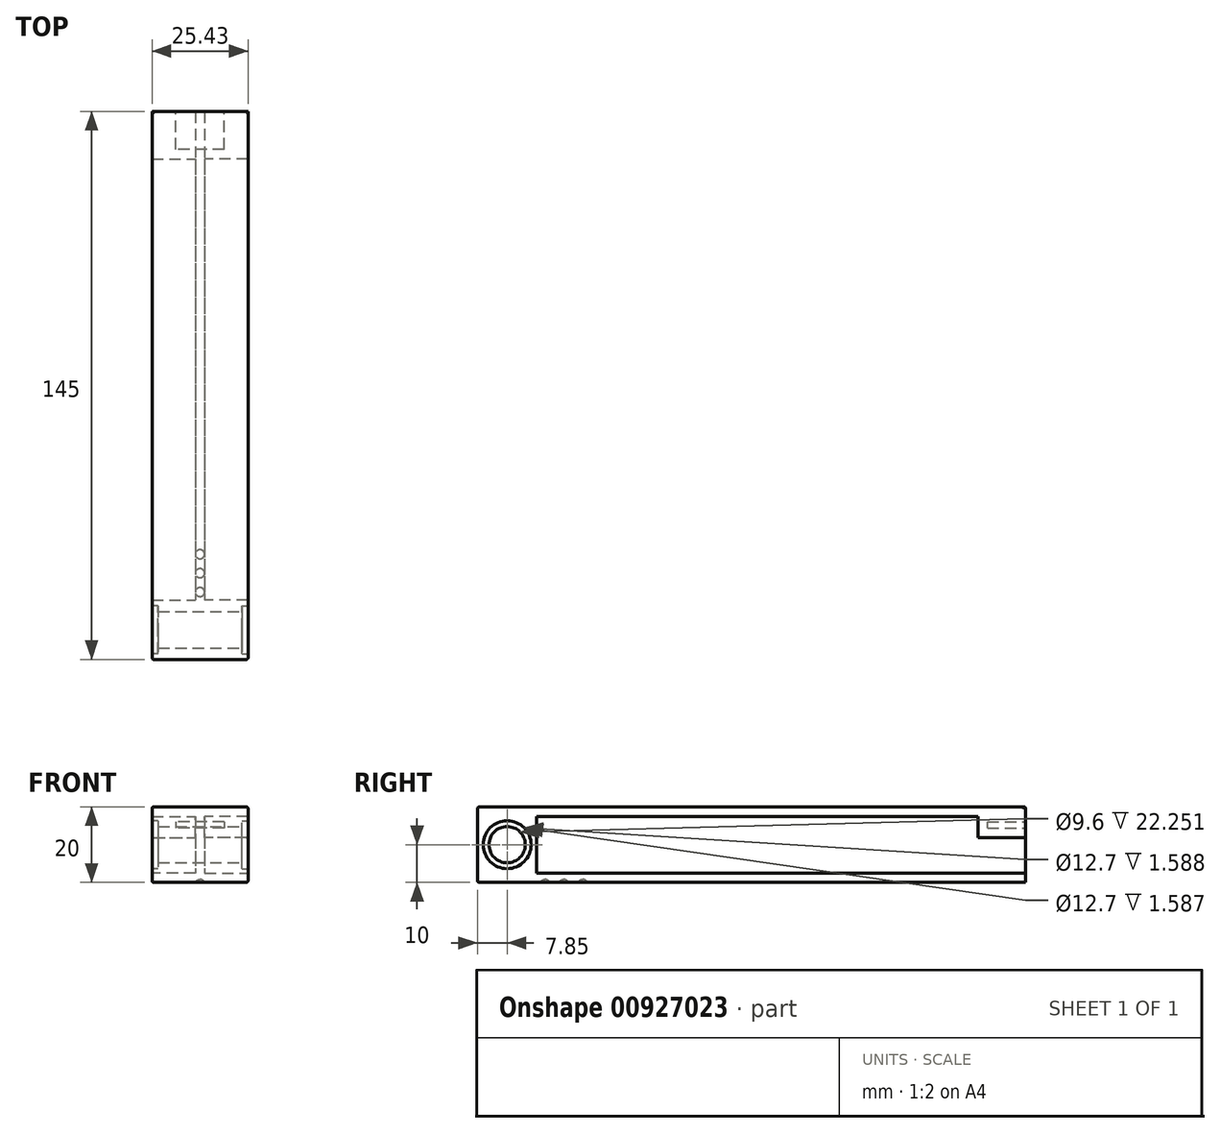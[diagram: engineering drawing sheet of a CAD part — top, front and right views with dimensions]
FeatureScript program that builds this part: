
annotation { "Feature Type Name" : "Feature", "Feature Type Description" : "" }
export const myFeature = defineFeature(function(context is Context, id is Id, definition is map)
    precondition{}
    {
        {
            var Q0;
            Q0=qCreatedBy(makeId("Front.planeOp"),FACE);
            var sketch = newSketch(context, id + "F0", { "sketchPlane" : qUnion([Q0])});
            skLineSegment(sketch, "E0", {"start": v(0, 0) * mm, "end": v(12.71, 0) * mm});
            skLineSegment(sketch, "E1", {"start": v(12.71, 0) * mm, "end": v(12.71, 20) * mm, "construction": true});
            skLineSegment(sketch, "E2", {"start": v(12.71, 20) * mm, "end": v(0, 20) * mm});
            skLineSegment(sketch, "E3", {"start": v(0, 20) * mm, "end": v(0, 17.5) * mm});
            skLineSegment(sketch, "E4", {"start": v(0, 17.5) * mm, "end": v(11.46, 17.5) * mm});
            skLineSegment(sketch, "E5", {"start": v(11.46, 17.5) * mm, "end": v(11.46, 2.5) * mm});
            skLineSegment(sketch, "E6", {"start": v(11.46, 2.5) * mm, "end": v(0, 2.5) * mm});
            skLineSegment(sketch, "E7", {"start": v(0, 2.5) * mm, "end": v(0, 0) * mm});
            skLineSegment(sketch, "E8.MirrorCS", {"start": v(12.71, 20) * mm, "end": v(25.43, 20) * mm});
            skLineSegment(sketch, "E9.MirrorCS", {"start": v(25.43, 20) * mm, "end": v(25.43, 17.5) * mm});
            skLineSegment(sketch, "E10.MirrorCS", {"start": v(25.43, 17.5) * mm, "end": v(13.96, 17.5) * mm});
            skLineSegment(sketch, "E11.MirrorCS", {"start": v(13.96, 17.5) * mm, "end": v(13.96, 2.5) * mm});
            skLineSegment(sketch, "E12.MirrorCS", {"start": v(13.96, 2.5) * mm, "end": v(25.43, 2.5) * mm});
            skLineSegment(sketch, "E13.MirrorCS", {"start": v(25.43, 2.5) * mm, "end": v(25.43, 0) * mm});
            skLineSegment(sketch, "E14.MirrorCS", {"start": v(25.43, 0) * mm, "end": v(12.71, 0) * mm});
            skSolve(sketch);
        }
        {
            var Q0;
            Q0=makeQuery(id+"F0.imprint","IMPRINT",FACE,{"disambiguationData":[TD([[makeQuery(id+"F0.imprint","IMPRINT",EDGE,{"derivedFrom":sQuery(id+"F0.wireOp",EDGE,"E0")}),1.0]])]});
            extrude(context, id + "F1", {"entities" : qUnion([Q0]), "oppositeDirection" : true, "depth" : 145 * mm, "offsetDistance" : 25 * mm});
        }
        {
            var Q0;
            Q0=makeQuery(id+"F1.opExtrude","SWEPT_FACE",FACE,{"disambiguationData":[OSD([sQuery(id+"F0.wireOp",EDGE,"E11.MirrorCS")])]});
            var sketch = newSketch(context, id + "F2", { "sketchPlane" : qUnion([Q0])});
            skLineSegment(sketch, "E15.bottom", {"start": v(0, 17.5) * mm, "end": v(15.7, 17.5) * mm});
            skLineSegment(sketch, "E15.top", {"start": v(0, 2.5) * mm, "end": v(15.7, 2.5) * mm});
            skLineSegment(sketch, "E15.left", {"start": v(0, 17.5) * mm, "end": v(0, 2.5) * mm});
            skLineSegment(sketch, "E15.right", {"start": v(15.7, 17.5) * mm, "end": v(15.7, 2.5) * mm});
            skSolve(sketch);
        }
        {
            var Q0;
            Q0=makeQuery(id+"F2.imprint","IMPRINT",FACE,{"disambiguationData":[TD([[makeQuery(id+"F2.imprint","IMPRINT",EDGE,{"derivedFrom":sQuery(id+"F2.wireOp",EDGE,"E15.bottom")}),1.0]])]});
            var Q1;
            Q1=makeQuery(id+"F1.opExtrude","SWEPT_FACE",FACE,{"disambiguationData":[OSD([sQuery(id+"F0.wireOp",EDGE,"E9.MirrorCS")])]});
            extrude(context, id + "F3", {"entities" : qUnion([Q0]), "operationType" : NewBodyOperationType.ADD, "endBound" : BoundingType.UP_TO_SURFACE, "depth" : 25 * mm, "endBoundEntityFace" : qUnion([Q1]), "offsetDistance" : 25 * mm});
        }
        {
            var Q0;
            Q0=makeQuery(id+"F1.opExtrude","SWEPT_FACE",FACE,{"disambiguationData":[OSD([sQuery(id+"F0.wireOp",EDGE,"E5")])]});
            var sketch = newSketch(context, id + "F4", { "sketchPlane" : qUnion([Q0])});
            skLineSegment(sketch, "E16.0", {"start": v(-15.7, 17.5) * mm, "end": v(-15.7, 2.5) * mm});
            skSolve(sketch);
        }
        {
            var Q0;
            {var subQ0=sQuery(id+"F4.wireOp",EDGE,"E16.0");Q0=makeQuery(id+"F4.imprint","IMPRINT",FACE,{"disambiguationData":[TD([[makeQuery(id+"F4.imprint","IMPRINT",EDGE,{"derivedFrom":subQ0}),1.0]])]});}
            var Q1;
            Q1=makeQuery(id+"F1.opExtrude","SWEPT_FACE",FACE,{"disambiguationData":[OSD([sQuery(id+"F0.wireOp",EDGE,"E3")])]});
            extrude(context, id + "F5", {"entities" : qUnion([Q0]), "operationType" : NewBodyOperationType.ADD, "endBound" : BoundingType.UP_TO_SURFACE, "depth" : 25 * mm, "endBoundEntityFace" : qUnion([Q1]), "offsetDistance" : 25 * mm});
        }
        {
            var Q0;
            Q0=makeQuery(id+"F3.boolean.opBoolean","MERGE",FACE,{"derivedFrom":[makeQuery(id+"F1.opExtrude","SWEPT_FACE",FACE,{"disambiguationData":[OSD([sQuery(id+"F0.wireOp",EDGE,"E9.MirrorCS")])]}),makeQuery(id+"F1.opExtrude","SWEPT_FACE",FACE,{"disambiguationData":[OSD([sQuery(id+"F0.wireOp",EDGE,"E13.MirrorCS")])]}),makeQuery(id+"F3.opExtrude","CAP_FACE",FACE,{"disambiguationData":[OSD([sQuery(id+"F2.wireOp",EDGE,"E15.bottom"),sQuery(id+"F2.wireOp",EDGE,"E15.top"),sQuery(id+"F2.wireOp",EDGE,"E15.left"),sQuery(id+"F2.wireOp",EDGE,"E15.right")])],"isStart":false})]});
            var sketch = newSketch(context, id + "F6", { "sketchPlane" : qUnion([Q0])});
            skLineSegment(sketch, "E17", {"start": v(0, 10) * mm, "end": v(15.7, 10) * mm});
            skCircle(sketch, "E18", {"center": v(7.85, 10) * mm, "radius": 4.8 * mm});
            skSolve(sketch);
        }
        {
            var Q0;
            {var subQ0=sQuery(id+"F6.wireOp",EDGE,"E18");var subQ1=sQuery(id+"F6.wireOp",EDGE,"E17");var subQ2=makeQuery(id+"F6.imprint","INTERSECT",VERTEX,{"disambiguationData":[OD(0.0)],"derivedFrom":[subQ1,subQ0]});Q0=makeQuery(id+"F6.imprint","IMPRINT",FACE,{"disambiguationData":[TD([[makeQuery(id+"F6.imprint","IMPRINT",EDGE,{"disambiguationData":[TD([[subQ2,-1.0]])],"derivedFrom":subQ1}),1.0]])]});}
            var Q1;
            {var subQ0=sQuery(id+"F6.wireOp",EDGE,"E18");var subQ1=sQuery(id+"F6.wireOp",EDGE,"E17");var subQ2=makeQuery(id+"F6.imprint","INTERSECT",VERTEX,{"disambiguationData":[OD(0.0)],"derivedFrom":[subQ1,subQ0]});Q1=makeQuery(id+"F6.imprint","IMPRINT",FACE,{"disambiguationData":[TD([[makeQuery(id+"F6.imprint","IMPRINT",EDGE,{"disambiguationData":[TD([[subQ2,-1.0]])],"derivedFrom":subQ1}),-1.0]])]});}
            extrude(context, id + "F7", {"entities" : qUnion([Q0, Q1]), "operationType" : NewBodyOperationType.REMOVE, "endBound" : BoundingType.THROUGH_ALL, "oppositeDirection" : true, "depth" : 1.2 * mm, "offsetDistance" : 25 * mm});
        }
        {
            var Q0;
            Q0=makeQuery(id+"F3.boolean.opBoolean","MERGE",FACE,{"derivedFrom":[makeQuery(id+"F1.opExtrude","SWEPT_FACE",FACE,{"disambiguationData":[OSD([sQuery(id+"F0.wireOp",EDGE,"E9.MirrorCS")])]}),makeQuery(id+"F1.opExtrude","SWEPT_FACE",FACE,{"disambiguationData":[OSD([sQuery(id+"F0.wireOp",EDGE,"E13.MirrorCS")])]}),makeQuery(id+"F3.opExtrude","CAP_FACE",FACE,{"disambiguationData":[OSD([sQuery(id+"F2.wireOp",EDGE,"E15.bottom"),sQuery(id+"F2.wireOp",EDGE,"E15.top"),sQuery(id+"F2.wireOp",EDGE,"E15.left"),sQuery(id+"F2.wireOp",EDGE,"E15.right")])],"isStart":false})]});
            var sketch = newSketch(context, id + "F8", { "sketchPlane" : qUnion([Q0])});
            skCircle(sketch, "E19", {"center": v(7.85, 10) * mm, "radius": 6.35 * mm});
            skSolve(sketch);
        }
        {
            var Q0;
            Q0=makeQuery(id+"F8.imprint","IMPRINT",FACE,{"disambiguationData":[TD([[makeQuery(id+"F8.imprint","IMPRINT",EDGE,{"derivedFrom":sQuery(id+"F8.wireOp",EDGE,"E19")}),1.0]])]});
            extrude(context, id + "F9", {"entities" : qUnion([Q0]), "operationType" : NewBodyOperationType.REMOVE, "oppositeDirection" : true, "depth" : 1.59 * mm, "offsetDistance" : 25 * mm});
        }
        {
            var Q0;
            Q0=makeQuery(id+"F1.opExtrude","SWEPT_FACE",FACE,{"disambiguationData":[OSD([sQuery(id+"F0.wireOp",EDGE,"E11.MirrorCS")])]});
            var sketch = newSketch(context, id + "F10", { "sketchPlane" : qUnion([Q0])});
            skLineSegment(sketch, "E20", {"start": v(135, 14.41) * mm, "end": v(145, 14.41) * mm});
            skLineSegment(sketch, "E21", {"start": v(145, 14.41) * mm, "end": v(145, 11.91) * mm});
            skLineSegment(sketch, "E22", {"start": v(145, 11.91) * mm, "end": v(132.5, 11.91) * mm});
            skLineSegment(sketch, "E23", {"start": v(132.5, 11.91) * mm, "end": v(132.5, 17.5) * mm});
            skLineSegment(sketch, "E24", {"start": v(132.5, 17.5) * mm, "end": v(145, 17.5) * mm});
            skLineSegment(sketch, "E25", {"start": v(145, 17.5) * mm, "end": v(145, 16) * mm});
            skLineSegment(sketch, "E26", {"start": v(145, 16) * mm, "end": v(135, 16) * mm});
            skLineSegment(sketch, "E27", {"start": v(135, 16) * mm, "end": v(135, 14.41) * mm});
            skSolve(sketch);
        }
        {
            var Q0;
            Q0=qSketchRegion(id+"FgvDUQmByhWsIWp_1",true);
            var Q1;
            Q1=makeQuery(id+"F10.imprint","IMPRINT",FACE,{"disambiguationData":[TD([[makeQuery(id+"F10.imprint","IMPRINT",EDGE,{"derivedFrom":sQuery(id+"F10.wireOp",EDGE,"E20")}),-1.0]])]});
            var Q2;
            Q2=makeQuery(id+"F3.boolean.opBoolean","MERGE",FACE,{"derivedFrom":[makeQuery(id+"F1.opExtrude","SWEPT_FACE",FACE,{"disambiguationData":[OSD([sQuery(id+"F0.wireOp",EDGE,"E9.MirrorCS")])]}),makeQuery(id+"F1.opExtrude","SWEPT_FACE",FACE,{"disambiguationData":[OSD([sQuery(id+"F0.wireOp",EDGE,"E13.MirrorCS")])]}),makeQuery(id+"F3.opExtrude","CAP_FACE",FACE,{"disambiguationData":[OSD([sQuery(id+"F2.wireOp",EDGE,"E15.bottom"),sQuery(id+"F2.wireOp",EDGE,"E15.top"),sQuery(id+"F2.wireOp",EDGE,"E15.left"),sQuery(id+"F2.wireOp",EDGE,"E15.right")])],"isStart":false})]});
            extrude(context, id + "F11", {"entities" : qUnion([Q0, Q1]), "operationType" : NewBodyOperationType.ADD, "endBound" : BoundingType.UP_TO_SURFACE, "depth" : 25 * mm, "endBoundEntityFace" : qUnion([Q2]), "offsetDistance" : 25 * mm});
        }
        {
            var Q0;
            Q0=makeQuery(id+"F1.opExtrude","SWEPT_FACE",FACE,{"disambiguationData":[OSD([sQuery(id+"F0.wireOp",EDGE,"E5")])]});
            var sketch = newSketch(context, id + "F12", { "sketchPlane" : qUnion([Q0])});
            skLineSegment(sketch, "E28.0", {"start": v(-132.5, 17.5) * mm, "end": v(-145, 17.5) * mm});
            skLineSegment(sketch, "E28.1", {"start": v(-132.5, 11.91) * mm, "end": v(-132.5, 17.5) * mm});
            skLineSegment(sketch, "E28.2", {"start": v(-145, 16) * mm, "end": v(-135, 16) * mm});
            skLineSegment(sketch, "E28.3", {"start": v(-135, 16) * mm, "end": v(-135, 14.41) * mm});
            skLineSegment(sketch, "E28.4", {"start": v(-135, 14.41) * mm, "end": v(-145, 14.41) * mm});
            skLineSegment(sketch, "E28.5", {"start": v(-145, 11.91) * mm, "end": v(-132.5, 11.91) * mm});
            skLineSegment(sketch, "E28.6", {"start": v(-145, 17.5) * mm, "end": v(-145, 16) * mm});
            skLineSegment(sketch, "E28.7", {"start": v(-145, 14.41) * mm, "end": v(-145, 11.91) * mm});
            skSolve(sketch);
        }
        {
            var Q0;
            Q0=makeQuery(id+"F12.imprint","IMPRINT",FACE,{"disambiguationData":[TD([[makeQuery(id+"F12.imprint","IMPRINT",EDGE,{"derivedFrom":sQuery(id+"F12.wireOp",EDGE,"E28.0")}),-1.0]])]});
            var Q1;
            Q1=makeQuery(id+"F5.boolean.opBoolean","MERGE",FACE,{"derivedFrom":[makeQuery(id+"F1.opExtrude","SWEPT_FACE",FACE,{"disambiguationData":[OSD([sQuery(id+"F0.wireOp",EDGE,"E3")])]}),makeQuery(id+"F1.opExtrude","SWEPT_FACE",FACE,{"disambiguationData":[OSD([sQuery(id+"F0.wireOp",EDGE,"E7")])]}),makeQuery(id+"F5.opExtrude","CAP_FACE",FACE,{"disambiguationData":[OSD([sQuery(id+"F0.wireOp",EDGE,"E4"),sQuery(id+"F0.wireOp",EDGE,"E5"),sQuery(id+"F0.wireOp",EDGE,"E6"),sQuery(id+"F4.wireOp",EDGE,"E16.0")])],"isStart":false})]});
            extrude(context, id + "F13", {"entities" : qUnion([Q0]), "operationType" : NewBodyOperationType.ADD, "endBound" : BoundingType.UP_TO_SURFACE, "depth" : 25 * mm, "endBoundEntityFace" : qUnion([Q1]), "offsetDistance" : 25 * mm});
        }
        {
            var Q0;
            {var subQ0=sQuery(id+"F0.wireOp",EDGE,"E5");Q0=makeQuery(id+"F13.boolean.opBoolean","MERGE",FACE,{"derivedFrom":[makeQuery(id+"F11.boolean.opBoolean","MERGE",FACE,{"derivedFrom":[makeQuery(id+"F1.opExtrude","CAP_FACE",FACE,{"disambiguationData":[OSD([sQuery(id+"F0.wireOp",EDGE,"E0"),sQuery(id+"F0.wireOp",EDGE,"E2"),sQuery(id+"F0.wireOp",EDGE,"E3"),sQuery(id+"F0.wireOp",EDGE,"E4"),subQ0,sQuery(id+"F0.wireOp",EDGE,"E6"),sQuery(id+"F0.wireOp",EDGE,"E7"),sQuery(id+"F0.wireOp",EDGE,"E8.MirrorCS"),sQuery(id+"F0.wireOp",EDGE,"E9.MirrorCS"),sQuery(id+"F0.wireOp",EDGE,"E10.MirrorCS"),sQuery(id+"F0.wireOp",EDGE,"E11.MirrorCS"),sQuery(id+"F0.wireOp",EDGE,"E12.MirrorCS"),sQuery(id+"F0.wireOp",EDGE,"E13.MirrorCS"),sQuery(id+"F0.wireOp",EDGE,"E14.MirrorCS")])],"isStart":false}),makeQuery(id+"F11.opExtrude","SWEPT_FACE",FACE,{"disambiguationData":[OSD([sQuery(id+"F10.wireOp",EDGE,"E21")])]})]}),makeQuery(id+"F13.opExtrude","SWEPT_FACE",FACE,{"disambiguationData":[OSD([subQ0])]})]});}
            var sketch = newSketch(context, id + "F14", { "sketchPlane" : qUnion([Q0])});
            skLineSegment(sketch, "E29.bottom", {"start": v(-25.43, 16) * mm, "end": v(-19.13, 16) * mm});
            skLineSegment(sketch, "E29.top", {"start": v(-25.43, 14.41) * mm, "end": v(-19.13, 14.41) * mm});
            skLineSegment(sketch, "E29.left", {"start": v(-25.43, 16) * mm, "end": v(-25.43, 14.41) * mm});
            skLineSegment(sketch, "E29.right", {"start": v(-19.13, 16) * mm, "end": v(-19.13, 14.41) * mm});
            skLineSegment(sketch, "E30.bottom", {"start": v(0, 16) * mm, "end": v(-6.3, 16) * mm});
            skLineSegment(sketch, "E30.top", {"start": v(0, 14.41) * mm, "end": v(-6.3, 14.41) * mm});
            skLineSegment(sketch, "E30.left", {"start": v(0, 16) * mm, "end": v(0, 14.41) * mm});
            skLineSegment(sketch, "E30.right", {"start": v(-6.3, 16) * mm, "end": v(-6.3, 14.41) * mm});
            skLineSegment(sketch, "E31.bottom", {"start": v(-11.46, 16) * mm, "end": v(-13.96, 16) * mm});
            skLineSegment(sketch, "E31.top", {"start": v(-11.46, 14.41) * mm, "end": v(-13.96, 14.41) * mm});
            skLineSegment(sketch, "E31.left", {"start": v(-11.46, 16) * mm, "end": v(-11.46, 14.41) * mm});
            skLineSegment(sketch, "E31.right", {"start": v(-13.96, 16) * mm, "end": v(-13.96, 14.41) * mm});
            skSolve(sketch);
        }
        {
            var Q0;
            Q0=makeQuery(id+"F14.imprint","IMPRINT",FACE,{"disambiguationData":[TD([[makeQuery(id+"F14.imprint","IMPRINT",EDGE,{"derivedFrom":sQuery(id+"F14.wireOp",EDGE,"E29.bottom")}),-1.0]])]});
            var Q1;
            Q1=makeQuery(id+"F14.imprint","IMPRINT",FACE,{"disambiguationData":[TD([[makeQuery(id+"F14.imprint","IMPRINT",EDGE,{"derivedFrom":sQuery(id+"F14.wireOp",EDGE,"E30.bottom")}),1.0]])]});
            extrude(context, id + "F15", {"entities" : qUnion([Q0, Q1]), "operationType" : NewBodyOperationType.ADD, "endBound" : BoundingType.UP_TO_NEXT, "oppositeDirection" : true, "depth" : 25 * mm, "offsetDistance" : 25 * mm});
        }
        {
            var Q0;
            Q0=makeQuery(id+"F14.imprint","IMPRINT",FACE,{"disambiguationData":[TD([[makeQuery(id+"F14.imprint","IMPRINT",EDGE,{"derivedFrom":sQuery(id+"F14.wireOp",EDGE,"E31.bottom")}),1.0]])]});
            var Q1;
            Q1=makeQuery(id+"F13.opExtrude","SWEPT_FACE",FACE,{"disambiguationData":[OSD([sQuery(id+"F12.wireOp",EDGE,"E28.3")])]});
            extrude(context, id + "F16", {"entities" : qUnion([Q0]), "operationType" : NewBodyOperationType.REMOVE, "endBound" : BoundingType.UP_TO_SURFACE, "oppositeDirection" : true, "depth" : 25 * mm, "endBoundEntityFace" : qUnion([Q1]), "offsetDistance" : 25 * mm});
        }
        {
            var Q0;
            Q0=makeQuery(id+"F7.boolean.opBoolean","MERGE",FACE,{"derivedFrom":[makeQuery(id+"F1.opExtrude","SWEPT_FACE",FACE,{"disambiguationData":[OSD([sQuery(id+"F0.wireOp",EDGE,"E0"),sQuery(id+"F0.wireOp",EDGE,"E14.MirrorCS")])]}),makeQuery(id+"F7.opExtrude","SWEPT_FACE",FACE,{"disambiguationData":[OSD([sQuery(id+"F6.wireOp",EDGE,"BxTbEPKq-brhq-NvGM-6ZMe-eOsR9q81uHOd.bottom")])]})]});
            var sketch = newSketch(context, id + "F17", { "sketchPlane" : qUnion([Q0])});
            skCircle(sketch, "E32", {"center": v(12.71, -17.85) * mm, "radius": 1.2 * mm});
            skLineSegment(sketch, "E33", {"start": v(0, 0) * mm, "end": v(25.43, 0) * mm, "construction": true});
            skLineSegment(sketch, "E34", {"start": v(12.71, -17.85) * mm, "end": v(12.71, 0) * mm, "construction": true});
            skCircle(sketch, "E35.0.1.0", {"center": v(12.71, -22.85) * mm, "radius": 1.2 * mm});
            skCircle(sketch, "E35.0.2.0", {"center": v(12.71, -27.85) * mm, "radius": 1.2 * mm});
            skLineSegment(sketch, "E35.direction1", {"start": v(12.71, -17.85) * mm, "end": v(31, -17.85) * mm, "construction": true});
            skLineSegment(sketch, "E35.direction2", {"start": v(12.71, -17.85) * mm, "end": v(12.71, -22.85) * mm, "construction": true});
            skSolve(sketch);
        }
        {
            var Q0;
            Q0=makeQuery(id+"F17.imprint","IMPRINT",FACE,{"disambiguationData":[TD([[makeQuery(id+"F17.imprint","IMPRINT",EDGE,{"derivedFrom":sQuery(id+"F17.wireOp",EDGE,"E32")}),1.0]])]});
            var Q1;
            Q1=makeQuery(id+"F17.imprint","IMPRINT",FACE,{"disambiguationData":[TD([[makeQuery(id+"F17.imprint","IMPRINT",EDGE,{"derivedFrom":sQuery(id+"F17.wireOp",EDGE,"E35.0.1.0")}),1.0]])]});
            var Q2;
            Q2=makeQuery(id+"F17.imprint","IMPRINT",FACE,{"disambiguationData":[TD([[makeQuery(id+"F17.imprint","IMPRINT",EDGE,{"derivedFrom":sQuery(id+"F17.wireOp",EDGE,"E35.0.2.0")}),1.0]])]});
            var Q3;
            Q3=makeQuery(id+"F17.imprint","IMPRINT",FACE,{"disambiguationData":[TD([[makeQuery(id+"F17.imprint","IMPRINT",EDGE,{"derivedFrom":sQuery(id+"F17.wireOp",EDGE,"E35.0.3.0")}),1.0]])]});
            var Q4;
            Q4=makeQuery(id+"F17.imprint","IMPRINT",FACE,{"disambiguationData":[TD([[makeQuery(id+"F17.imprint","IMPRINT",EDGE,{"derivedFrom":sQuery(id+"F17.wireOp",EDGE,"E35.0.4.0")}),1.0]])]});
            var Q5;
            Q5=makeQuery(id+"F17.imprint","IMPRINT",FACE,{"disambiguationData":[TD([[makeQuery(id+"F17.imprint","IMPRINT",EDGE,{"derivedFrom":sQuery(id+"F17.wireOp",EDGE,"E35.0.5.0")}),1.0]])]});
            var Q6;
            Q6=makeQuery(id+"F17.imprint","IMPRINT",FACE,{"disambiguationData":[TD([[makeQuery(id+"F17.imprint","IMPRINT",EDGE,{"derivedFrom":sQuery(id+"F17.wireOp",EDGE,"E35.0.6.0")}),1.0]])]});
            var Q7;
            Q7=makeQuery(id+"F17.imprint","IMPRINT",FACE,{"disambiguationData":[TD([[makeQuery(id+"F17.imprint","IMPRINT",EDGE,{"derivedFrom":sQuery(id+"F17.wireOp",EDGE,"E35.0.7.0")}),1.0]])]});
            var Q8;
            Q8=makeQuery(id+"F17.imprint","IMPRINT",FACE,{"disambiguationData":[TD([[makeQuery(id+"F17.imprint","IMPRINT",EDGE,{"derivedFrom":sQuery(id+"F17.wireOp",EDGE,"E35.0.8.0")}),1.0]])]});
            var Q9;
            Q9=makeQuery(id+"F17.imprint","IMPRINT",FACE,{"disambiguationData":[TD([[makeQuery(id+"F17.imprint","IMPRINT",EDGE,{"derivedFrom":sQuery(id+"F17.wireOp",EDGE,"E35.0.9.0")}),1.0]])]});
            var Q10;
            Q10=makeQuery(id+"F17.imprint","IMPRINT",FACE,{"disambiguationData":[TD([[makeQuery(id+"F17.imprint","IMPRINT",EDGE,{"derivedFrom":sQuery(id+"F17.wireOp",EDGE,"E35.0.10.0")}),1.0]])]});
            var Q11;
            Q11=makeQuery(id+"F17.imprint","IMPRINT",FACE,{"disambiguationData":[TD([[makeQuery(id+"F17.imprint","IMPRINT",EDGE,{"derivedFrom":sQuery(id+"F17.wireOp",EDGE,"E35.0.11.0")}),1.0]])]});
            extrude(context, id + "F18", {"entities" : qUnion([Q0, Q1, Q2, Q3, Q4, Q5, Q6, Q7, Q8, Q9, Q10, Q11]), "operationType" : NewBodyOperationType.REMOVE, "oppositeDirection" : true, "depth" : 0.8 * mm, "offsetDistance" : 25 * mm});
        }
        {
            var Q0;
            Q0=makeQuery(id+"F18.boolean.opBoolean","COPY",EDGE,{"derivedFrom":makeQuery(id+"F18.opExtrude","CAP_EDGE",EDGE,{"disambiguationData":[OSD([sQuery(id+"F17.wireOp",EDGE,"E35.0.11.0")])],"isStart":false})});
            var Q1;
            Q1=makeQuery(id+"F18.boolean.opBoolean","COPY",EDGE,{"derivedFrom":makeQuery(id+"F18.opExtrude","CAP_EDGE",EDGE,{"disambiguationData":[OSD([sQuery(id+"F17.wireOp",EDGE,"E35.0.10.0")])],"isStart":false})});
            var Q2;
            Q2=makeQuery(id+"F18.boolean.opBoolean","COPY",EDGE,{"derivedFrom":makeQuery(id+"F18.opExtrude","CAP_EDGE",EDGE,{"disambiguationData":[OSD([sQuery(id+"F17.wireOp",EDGE,"E35.0.9.0")])],"isStart":false})});
            var Q3;
            Q3=makeQuery(id+"F18.boolean.opBoolean","COPY",EDGE,{"derivedFrom":makeQuery(id+"F18.opExtrude","CAP_EDGE",EDGE,{"disambiguationData":[OSD([sQuery(id+"F17.wireOp",EDGE,"E35.0.8.0")])],"isStart":false})});
            var Q4;
            Q4=makeQuery(id+"F18.boolean.opBoolean","COPY",EDGE,{"derivedFrom":makeQuery(id+"F18.opExtrude","CAP_EDGE",EDGE,{"disambiguationData":[OSD([sQuery(id+"F17.wireOp",EDGE,"E35.0.7.0")])],"isStart":false})});
            var Q5;
            Q5=makeQuery(id+"F18.boolean.opBoolean","COPY",EDGE,{"derivedFrom":makeQuery(id+"F18.opExtrude","CAP_EDGE",EDGE,{"disambiguationData":[OSD([sQuery(id+"F17.wireOp",EDGE,"E35.0.6.0")])],"isStart":false})});
            var Q6;
            Q6=makeQuery(id+"F18.boolean.opBoolean","COPY",EDGE,{"derivedFrom":makeQuery(id+"F18.opExtrude","CAP_EDGE",EDGE,{"disambiguationData":[OSD([sQuery(id+"F17.wireOp",EDGE,"E35.0.5.0")])],"isStart":false})});
            var Q7;
            Q7=makeQuery(id+"F18.boolean.opBoolean","COPY",EDGE,{"derivedFrom":makeQuery(id+"F18.opExtrude","CAP_EDGE",EDGE,{"disambiguationData":[OSD([sQuery(id+"F17.wireOp",EDGE,"E35.0.4.0")])],"isStart":false})});
            var Q8;
            Q8=makeQuery(id+"F18.boolean.opBoolean","COPY",EDGE,{"derivedFrom":makeQuery(id+"F18.opExtrude","CAP_EDGE",EDGE,{"disambiguationData":[OSD([sQuery(id+"F17.wireOp",EDGE,"E35.0.3.0")])],"isStart":false})});
            var Q9;
            Q9=makeQuery(id+"F18.boolean.opBoolean","COPY",EDGE,{"derivedFrom":makeQuery(id+"F18.opExtrude","CAP_EDGE",EDGE,{"disambiguationData":[OSD([sQuery(id+"F17.wireOp",EDGE,"E35.0.2.0")])],"isStart":false})});
            var Q10;
            Q10=makeQuery(id+"F18.boolean.opBoolean","COPY",EDGE,{"derivedFrom":makeQuery(id+"F18.opExtrude","CAP_EDGE",EDGE,{"disambiguationData":[OSD([sQuery(id+"F17.wireOp",EDGE,"E35.0.1.0")])],"isStart":false})});
            var Q11;
            Q11=makeQuery(id+"F18.boolean.opBoolean","COPY",EDGE,{"derivedFrom":makeQuery(id+"F18.opExtrude","CAP_EDGE",EDGE,{"disambiguationData":[OSD([sQuery(id+"F17.wireOp",EDGE,"E32")])],"isStart":false})});
            fillet(context, id + "F19", {"entities" : qUnion([Q0, Q1, Q2, Q3, Q4, Q5, Q6, Q7, Q8, Q9, Q10, Q11]), "radius" : 1.2 * mm, "tangentPropagation" : true, "allowEdgeOverflow" : false});
        }
        {
            var Q0;
            Q0=makeQuery(id+"F16.boolean.opBoolean","COPY",EDGE,{"derivedFrom":makeQuery(id+"F16.opExtrude","SWEPT_EDGE",EDGE,{"disambiguationData":[OSD([sQuery(id+"F0.wireOp",EDGE,"E2"),sQuery(id+"F0.wireOp",EDGE,"E8.MirrorCS"),sQuery(id+"F14.wireOp",EDGE,"0EWzOAzJ-FitD-dZOc-zAf9-mVBQwacMPEmS"),sQuery(id+"F14.wireOp",EDGE,"3a1VO8J1-pKlq-Oro1-SVKx-ygcU3vKSFJe3")])]})});
            var Q1;
            Q1=makeQuery(id+"F16.boolean.opBoolean","COPY",EDGE,{"derivedFrom":makeQuery(id+"F16.opExtrude","SWEPT_EDGE",EDGE,{"disambiguationData":[OSD([sQuery(id+"F0.wireOp",EDGE,"E10.MirrorCS"),sQuery(id+"F14.wireOp",EDGE,"0EWzOAzJ-FitD-dZOc-zAf9-mVBQwacMPEmS"),sQuery(id+"F14.wireOp",EDGE,"chC3mlCo-7ysk-qYXu-zDaA-1en8GhesRIkC")])]})});
            var Q2;
            Q2=makeQuery(id+"F16.boolean.opBoolean","COPY",EDGE,{"derivedFrom":makeQuery(id+"F16.opExtrude","SWEPT_EDGE",EDGE,{"disambiguationData":[OSD([sQuery(id+"F0.wireOp",EDGE,"E2"),sQuery(id+"F0.wireOp",EDGE,"E8.MirrorCS"),sQuery(id+"F14.wireOp",EDGE,"ceRFCyRu-8BYw-4e90-c2ns-8t8g8dATU1da"),sQuery(id+"F14.wireOp",EDGE,"3a1VO8J1-pKlq-Oro1-SVKx-ygcU3vKSFJe3")])]})});
            var Q3;
            Q3=makeQuery(id+"F16.boolean.opBoolean","COPY",EDGE,{"derivedFrom":makeQuery(id+"F16.opExtrude","SWEPT_EDGE",EDGE,{"disambiguationData":[OSD([sQuery(id+"F0.wireOp",EDGE,"E4"),sQuery(id+"F14.wireOp",EDGE,"va9mFEuU-5wCR-oyVD-Y4VQ-zi8C2ubbxEkB"),sQuery(id+"F14.wireOp",EDGE,"ceRFCyRu-8BYw-4e90-c2ns-8t8g8dATU1da")])]})});
            var Q4;
            Q4=makeQuery(id+"F16.boolean.opBoolean","COPY",EDGE,{"derivedFrom":makeQuery(id+"F16.opExtrude","CAP_EDGE",EDGE,{"disambiguationData":[OSD([sQuery(id+"F14.wireOp",EDGE,"0EWzOAzJ-FitD-dZOc-zAf9-mVBQwacMPEmS")])],"isStart":true})});
            var Q5;
            Q5=makeQuery(id+"F16.boolean.opBoolean","COPY",EDGE,{"derivedFrom":makeQuery(id+"F16.opExtrude","CAP_EDGE",EDGE,{"disambiguationData":[OSD([sQuery(id+"F14.wireOp",EDGE,"ceRFCyRu-8BYw-4e90-c2ns-8t8g8dATU1da")])],"isStart":true})});
            var Q6;
            Q6=makeQuery(id+"F1.opExtrude","CAP_EDGE",EDGE,{"disambiguationData":[OSD([sQuery(id+"F0.wireOp",EDGE,"E10.MirrorCS")])],"isStart":false});
            var Q7;
            Q7=makeQuery(id+"F15.opExtrude","CAP_EDGE",EDGE,{"disambiguationData":[OSD([sQuery(id+"F14.wireOp",EDGE,"407AdA0n-u7l6-K8e3-t0Ld-mCcvsT80spbc.right")])],"isStart":true});
            var Q8;
            Q8=makeQuery(id+"F16.boolean.opBoolean","MERGE",EDGE,{"derivedFrom":[makeQuery(id+"F11.opExtrude","SWEPT_EDGE",EDGE,{"disambiguationData":[OSD([sQuery(id+"F10.wireOp",EDGE,"E20"),sQuery(id+"F10.wireOp",EDGE,"E21"),sQuery(id+"F10.wireOp",EDGE,"vd0n2bWI-2w59-8aZA-U7OC-NVR1PWX096RI")])]}),makeQuery(id+"F13.opExtrude","SWEPT_EDGE",EDGE,{"disambiguationData":[OSD([sQuery(id+"F0.wireOp",EDGE,"E5"),sQuery(id+"FgvDUQmByhWsIWp_1.wireOp",EDGE,"494ee2e7-549b-4880-af38-ae2305f98c9e.0")])]})],"fromTools":[makeQuery(id+"F16.opExtrude","CAP_EDGE",EDGE,{"disambiguationData":[OSD([sQuery(id+"F14.wireOp",EDGE,"XO4pMfx4-b2yW-cmLo-uSqd-TG0deKBsu0AE")])],"isStart":true})]});
            var Q9;
            Q9=makeQuery(id+"F15.opExtrude","CAP_EDGE",EDGE,{"disambiguationData":[OSD([sQuery(id+"F14.wireOp",EDGE,"t20VARuM-3wV1-ago3-HXmc-T0NwQvSHDK2S.right")])],"isStart":true});
            var Q10;
            Q10=makeQuery(id+"F1.opExtrude","CAP_EDGE",EDGE,{"disambiguationData":[OSD([sQuery(id+"F0.wireOp",EDGE,"E4")])],"isStart":false});
            var Q11;
            {var subQ3=sQuery(id+"F0.wireOp",EDGE,"E8.MirrorCS");var subQ6=sQuery(id+"F0.wireOp",EDGE,"E3");var subQ7=sQuery(id+"F0.wireOp",EDGE,"E2");Q11=makeQuery(id+"F16.boolean.opBoolean","SPLIT",EDGE,{"disambiguationData":[TD([makeQuery(id+"F1.opExtrude","SWEPT_FACE",FACE,{"disambiguationData":[OSD([subQ6])]})])],"derivedFrom":makeQuery(id+"F1.opExtrude","CAP_EDGE",EDGE,{"disambiguationData":[OSD([subQ7,subQ3])],"isStart":false})});}
            var Q12;
            {var subQ4=sQuery(id+"F0.wireOp",EDGE,"E9.MirrorCS");var subQ5=sQuery(id+"F0.wireOp",EDGE,"E8.MirrorCS");var subQ6=sQuery(id+"F0.wireOp",EDGE,"E2");Q12=makeQuery(id+"F16.boolean.opBoolean","SPLIT",EDGE,{"disambiguationData":[TD([makeQuery(id+"F1.opExtrude","SWEPT_FACE",FACE,{"disambiguationData":[OSD([subQ4])]})])],"derivedFrom":makeQuery(id+"F1.opExtrude","CAP_EDGE",EDGE,{"disambiguationData":[OSD([subQ6,subQ5])],"isStart":false})});}
            fillet(context, id + "F20", {"entities" : qUnion([Q0, Q1, Q2, Q3, Q4, Q5, Q6, Q7, Q8, Q9, Q10, Q11, Q12]), "radius" : 0.3 * mm, "tangentPropagation" : true, "allowEdgeOverflow" : false});
        }
        {
            var Q0;
            Q0=makeQuery(id+"F3.boolean.opBoolean","MERGE",EDGE,{"derivedFrom":[makeQuery(id+"F1.opExtrude","CAP_EDGE",EDGE,{"disambiguationData":[OSD([sQuery(id+"F0.wireOp",EDGE,"E9.MirrorCS")])],"isStart":true}),makeQuery(id+"F1.opExtrude","CAP_EDGE",EDGE,{"disambiguationData":[OSD([sQuery(id+"F0.wireOp",EDGE,"E13.MirrorCS")])],"isStart":true}),makeQuery(id+"F3.opExtrude","CAP_EDGE",EDGE,{"disambiguationData":[OSD([sQuery(id+"F2.wireOp",EDGE,"E15.left")])],"isStart":false})]});
            var Q1;
            Q1=makeQuery(id+"F1.opExtrude","CAP_EDGE",EDGE,{"disambiguationData":[OSD([sQuery(id+"F0.wireOp",EDGE,"E2"),sQuery(id+"F0.wireOp",EDGE,"E8.MirrorCS")])],"isStart":true});
            var Q2;
            Q2=makeQuery(id+"F5.boolean.opBoolean","MERGE",EDGE,{"derivedFrom":[makeQuery(id+"F1.opExtrude","CAP_EDGE",EDGE,{"disambiguationData":[OSD([sQuery(id+"F0.wireOp",EDGE,"E3")])],"isStart":true}),makeQuery(id+"F1.opExtrude","CAP_EDGE",EDGE,{"disambiguationData":[OSD([sQuery(id+"F0.wireOp",EDGE,"E7")])],"isStart":true}),makeQuery(id+"F5.opExtrude","CAP_EDGE",EDGE,{"disambiguationData":[OSD([sQuery(id+"F0.wireOp",EDGE,"E5")])],"isStart":false})]});
            var Q3;
            {var subQ1=sQuery(id+"F0.wireOp",EDGE,"E14.MirrorCS");var subQ2=sQuery(id+"F0.wireOp",EDGE,"E0");var subQ3=sQuery(id+"F0.wireOp",EDGE,"E9.MirrorCS");Q3=makeQuery(id+"F7.boolean.opBoolean","SPLIT",EDGE,{"disambiguationData":[TD([makeQuery(id+"F1.opExtrude","SWEPT_FACE",FACE,{"disambiguationData":[OSD([subQ3])]})])],"derivedFrom":makeQuery(id+"F1.opExtrude","CAP_EDGE",EDGE,{"disambiguationData":[OSD([subQ2,subQ1])],"isStart":true})});}
            var Q4;
            {var subQ1=sQuery(id+"F0.wireOp",EDGE,"E3");var subQ2=sQuery(id+"F0.wireOp",EDGE,"E14.MirrorCS");var subQ3=sQuery(id+"F0.wireOp",EDGE,"E0");Q4=makeQuery(id+"F7.boolean.opBoolean","SPLIT",EDGE,{"disambiguationData":[TD([makeQuery(id+"F1.opExtrude","SWEPT_FACE",FACE,{"disambiguationData":[OSD([subQ1])]})])],"derivedFrom":makeQuery(id+"F1.opExtrude","CAP_EDGE",EDGE,{"disambiguationData":[OSD([subQ3,subQ2])],"isStart":true})});}
            var Q5;
            Q5=makeQuery(id+"F7.opExtrude","CAP_EDGE",EDGE,{"disambiguationData":[OSD([sQuery(id+"F6.wireOp",EDGE,"Acf1WHJB-aBRB-DRkU-axKS-Z7H7J4MPcPoX.bottom")])],"isStart":false});
            var Q6;
            Q6=makeQuery(id+"F9.boolean.opBoolean","MERGE",EDGE,{"derivedFrom":[makeQuery(id+"F7.opExtrude","CAP_EDGE",EDGE,{"disambiguationData":[OSD([sQuery(id+"F6.wireOp",EDGE,"Acf1WHJB-aBRB-DRkU-axKS-Z7H7J4MPcPoX.right")])],"isStart":false}),makeQuery(id+"F9.opExtrude","CAP_EDGE",EDGE,{"disambiguationData":[OSD([sQuery(id+"F8.wireOp",EDGE,"NqeFW8ns-KF7f-yHsn-Wv7r-Wm2yH51Kyre3")])],"isStart":false})]});
            var Q7;
            Q7=makeQuery(id+"F9.boolean.opBoolean","MERGE",EDGE,{"derivedFrom":[makeQuery(id+"F7.opExtrude","CAP_EDGE",EDGE,{"disambiguationData":[OSD([sQuery(id+"F6.wireOp",EDGE,"Acf1WHJB-aBRB-DRkU-axKS-Z7H7J4MPcPoX.left")])],"isStart":false}),makeQuery(id+"F9.opExtrude","CAP_EDGE",EDGE,{"disambiguationData":[OSD([sQuery(id+"F8.wireOp",EDGE,"NqeFW8ns-KF7f-yHsn-Wv7r-Wm2yH51Kyre3")])],"isStart":true})]});
            var Q8;
            Q8=makeQuery(id+"F1.opExtrude","SWEPT_EDGE",EDGE,{"disambiguationData":[OSD([sQuery(id+"F0.wireOp",EDGE,"E8.MirrorCS"),sQuery(id+"F0.wireOp",EDGE,"E9.MirrorCS")])]});
            var Q9;
            Q9=makeQuery(id+"F1.opExtrude","SWEPT_EDGE",EDGE,{"disambiguationData":[OSD([sQuery(id+"F0.wireOp",EDGE,"E2"),sQuery(id+"F0.wireOp",EDGE,"E3")])]});
            var Q10;
            Q10=makeQuery(id+"F1.opExtrude","SWEPT_EDGE",EDGE,{"disambiguationData":[OSD([sQuery(id+"F0.wireOp",EDGE,"E13.MirrorCS"),sQuery(id+"F0.wireOp",EDGE,"E14.MirrorCS")])]});
            var Q11;
            Q11=makeQuery(id+"F1.opExtrude","SWEPT_EDGE",EDGE,{"disambiguationData":[OSD([sQuery(id+"F0.wireOp",EDGE,"E0"),sQuery(id+"F0.wireOp",EDGE,"E7")])]});
            fillet(context, id + "F21", {"entities" : qUnion([Q0, Q1, Q2, Q3, Q4, Q5, Q6, Q7, Q8, Q9, Q10, Q11]), "radius" : 0.5 * mm, "tangentPropagation" : true, "allowEdgeOverflow" : false});
        }
        {
            var Q0;
            Q0=makeQuery(id+"F15.boolean.opBoolean","MERGE",FACE,{"derivedFrom":[makeQuery(id+"F13.boolean.opBoolean","MERGE",FACE,{"derivedFrom":[makeQuery(id+"F5.boolean.opBoolean","MERGE",FACE,{"derivedFrom":[makeQuery(id+"F1.opExtrude","SWEPT_FACE",FACE,{"disambiguationData":[OSD([sQuery(id+"F0.wireOp",EDGE,"E3")])]}),makeQuery(id+"F1.opExtrude","SWEPT_FACE",FACE,{"disambiguationData":[OSD([sQuery(id+"F0.wireOp",EDGE,"E7")])]}),makeQuery(id+"F5.opExtrude","CAP_FACE",FACE,{"disambiguationData":[OSD([sQuery(id+"F0.wireOp",EDGE,"E4"),sQuery(id+"F0.wireOp",EDGE,"E5"),sQuery(id+"F0.wireOp",EDGE,"E6"),sQuery(id+"F4.wireOp",EDGE,"E16.0")])],"isStart":false})]}),makeQuery(id+"F13.opExtrude","CAP_FACE",FACE,{"disambiguationData":[OSD([sQuery(id+"F12.wireOp",EDGE,"E28.0"),sQuery(id+"F12.wireOp",EDGE,"E28.1"),sQuery(id+"F12.wireOp",EDGE,"E28.2"),sQuery(id+"F12.wireOp",EDGE,"E28.3"),sQuery(id+"F12.wireOp",EDGE,"E28.4"),sQuery(id+"F12.wireOp",EDGE,"E28.5"),sQuery(id+"F12.wireOp",EDGE,"E28.6"),sQuery(id+"F12.wireOp",EDGE,"E28.7")])],"isStart":false})]}),makeQuery(id+"F15.opExtrude","SWEPT_FACE",FACE,{"disambiguationData":[OSD([sQuery(id+"F14.wireOp",EDGE,"E30.left")])]})]});
            var sketch = newSketch(context, id + "F22", { "sketchPlane" : qUnion([Q0])});
            skCircle(sketch, "E36", {"center": v(-7.85, 10) * mm, "radius": 6.35 * mm});
            skSolve(sketch);
        }
        {
            var Q0;
            Q0=makeQuery(id+"F22.imprint","IMPRINT",FACE,{"disambiguationData":[TD([[makeQuery(id+"F22.imprint","IMPRINT",EDGE,{"derivedFrom":sQuery(id+"F22.wireOp",EDGE,"E36")}),1.0]])]});
            extrude(context, id + "F23", {"entities" : qUnion([Q0]), "operationType" : NewBodyOperationType.REMOVE, "oppositeDirection" : true, "depth" : 1.59 * mm, "offsetDistance" : 25 * mm});
        }
    });
